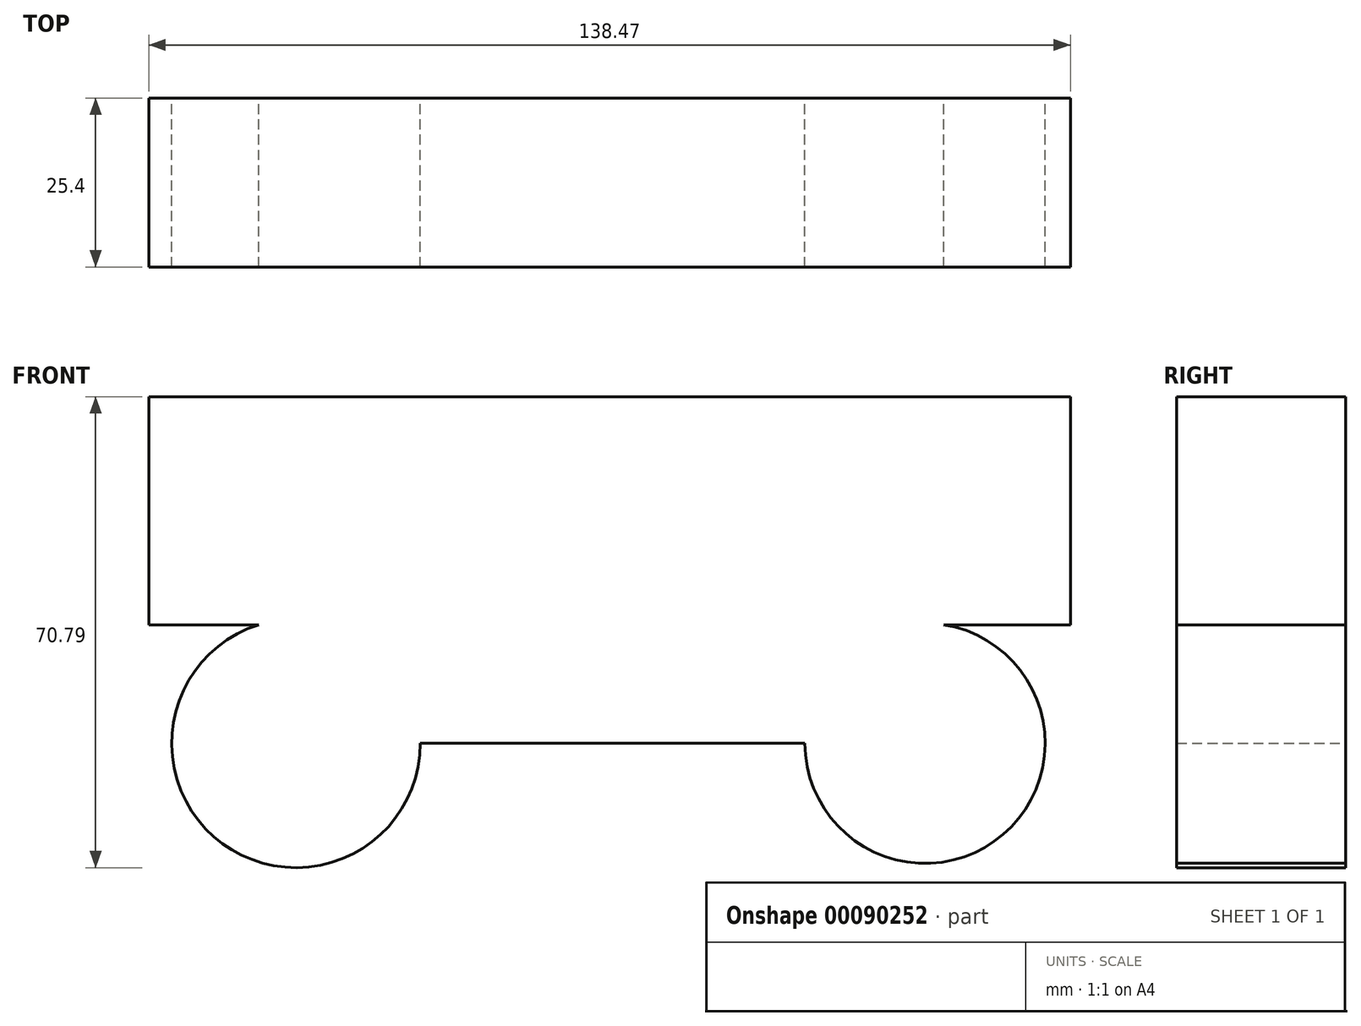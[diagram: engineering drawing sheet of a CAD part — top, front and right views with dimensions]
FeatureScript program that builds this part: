
annotation { "Feature Type Name" : "Feature", "Feature Type Description" : "" }
export const myFeature = defineFeature(function(context is Context, id is Id, definition is map)
    precondition{}
    {
        {
            var Q0;
            Q0=qCreatedBy(makeId("Front.planeOp"),FACE);
            var sketch = newSketch(context, id + "F0", { "sketchPlane" : qUnion([Q0])});
            skArc(sketch, "E0", {"start": v(-48.45, 17.83) * mm, "mid": v(-42.84, -18.69) * mm, "end": v(-37.23, 17.83) * mm});
            skArc(sketch, "E1", {"start": v(48.88, 17.83) * mm, "mid": v(51.68, -18.05) * mm, "end": v(54.49, 17.83) * mm});
            skLineSegment(sketch, "E2", {"start": v(-42.84, 0) * mm, "end": v(51.68, 0) * mm});
            skLineSegment(sketch, "E3.bottom", {"start": v(-64.95, 17.83) * mm, "end": v(73.52, 17.83) * mm});
            skLineSegment(sketch, "E3.top", {"start": v(-64.95, 52.1) * mm, "end": v(73.52, 52.1) * mm});
            skLineSegment(sketch, "E3.left", {"start": v(-64.95, 17.83) * mm, "end": v(-64.95, 52.1) * mm});
            skLineSegment(sketch, "E3.right", {"start": v(73.52, 17.83) * mm, "end": v(73.52, 52.1) * mm});
            skLineSegment(sketch, "E4.right", {"start": v(-41.68, 18.67) * mm, "end": v(-41.68, 18.65) * mm});
            skSolve(sketch);
        }
        {
            var Q0;
            Q0 = qSketchRegion(id + "F0", true);
            extrude(context, id + "F1", {"entities" : qUnion([Q0]), "depth" : 25.4 * mm});
        }
    });
